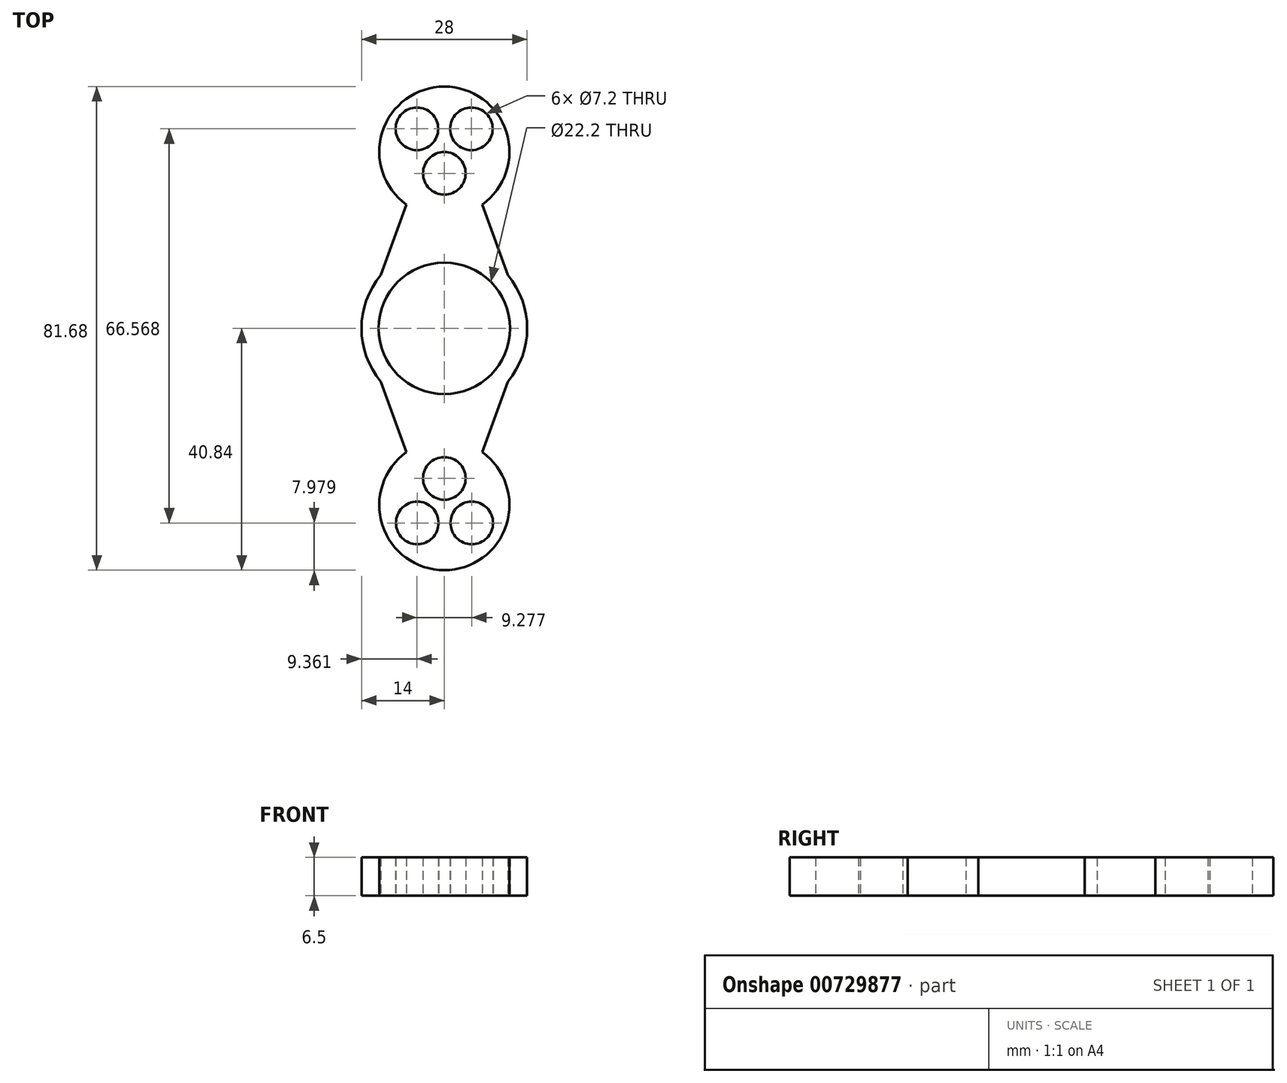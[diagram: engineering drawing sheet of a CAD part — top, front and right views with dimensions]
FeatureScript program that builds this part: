
annotation { "Feature Type Name" : "Feature", "Feature Type Description" : "" }
export const myFeature = defineFeature(function(context is Context, id is Id, definition is map)
    precondition{}
    {
        {
            var Q0;
            Q0=qCreatedBy(makeId("Top.planeOp"),FACE);
            var sketch = newSketch(context, id + "F0", { "sketchPlane" : qUnion([Q0])});
            skCircle(sketch, "E0", {"center": v(0, 0) * mm, "radius": 11.1 * mm});
            skCircle(sketch, "E1", {"center": v(0, 0) * mm, "radius": 14 * mm});
            skLineSegment(sketch, "E2", {"start": v(-14, 0) * mm, "end": v(0, 38.49) * mm});
            skLineSegment(sketch, "E3", {"start": v(0, 38.49) * mm, "end": v(14, 0) * mm});
            skCircle(sketch, "E4", {"center": v(0, 29.84) * mm, "radius": 11 * mm});
            skLineSegment(sketch, "E5", {"start": v(14, 0) * mm, "end": v(0, -38.49) * mm});
            skLineSegment(sketch, "E6", {"start": v(0, -38.49) * mm, "end": v(-14, 0) * mm});
            skCircle(sketch, "E7", {"center": v(0, -29.84) * mm, "radius": 11 * mm});
            skCircle(sketch, "E8", {"center": v(4.58, 33.7) * mm, "radius": 3.6 * mm});
            skCircle(sketch, "E9", {"center": v(-4.64, 33.7) * mm, "radius": 3.6 * mm});
            skCircle(sketch, "E10", {"center": v(0, 26.19) * mm, "radius": 3.6 * mm});
            skCircle(sketch, "E11", {"center": v(-4.58, -32.86) * mm, "radius": 3.6 * mm});
            skCircle(sketch, "E12", {"center": v(4.64, -32.86) * mm, "radius": 3.6 * mm});
            skCircle(sketch, "E13", {"center": v(0, -25.34) * mm, "radius": 3.6 * mm});
            skSolve(sketch);
        }
        {
            var Q0;
            Q0=makeQuery(id+"F0.imprint","IMPRINT",FACE,{"disambiguationData":[TD([[makeQuery(id+"F0.imprint","IMPRINT",EDGE,{"derivedFrom":sQuery(id+"F0.wireOp",EDGE,"E0")}),-1.0]])]});
            var Q1;
            {var subQ0=sQuery(id+"F0.wireOp",EDGE,"E2");var subQ1=sQuery(id+"F0.wireOp",EDGE,"E1");var subQ3=makeQuery(id+"F0.imprint","INTERSECT",VERTEX,{"derivedFrom":[subQ1,subQ0]});Q1=makeQuery(id+"F0.imprint","IMPRINT",FACE,{"disambiguationData":[TD([[makeQuery(id+"F0.imprint","IMPRINT",EDGE,{"disambiguationData":[TD([[subQ3,-1.0]])],"derivedFrom":subQ1}),1.0]])]});}
            var Q2;
            {var subQ0=sQuery(id+"F0.wireOp",EDGE,"E6");var subQ1=sQuery(id+"F0.wireOp",EDGE,"E1");var subQ3=makeQuery(id+"F0.imprint","INTERSECT",VERTEX,{"derivedFrom":[subQ1,subQ0]});Q2=makeQuery(id+"F0.imprint","IMPRINT",FACE,{"disambiguationData":[TD([[makeQuery(id+"F0.imprint","IMPRINT",EDGE,{"disambiguationData":[TD([[subQ3,1.0]])],"derivedFrom":subQ1}),1.0]])]});}
            var Q3;
            {var subQ0=sQuery(id+"F0.wireOp",EDGE,"E5");var subQ1=sQuery(id+"F0.wireOp",EDGE,"E1");var subQ3=makeQuery(id+"F0.imprint","INTERSECT",VERTEX,{"derivedFrom":[subQ1,subQ0]});Q3=makeQuery(id+"F0.imprint","IMPRINT",FACE,{"disambiguationData":[TD([[makeQuery(id+"F0.imprint","IMPRINT",EDGE,{"disambiguationData":[TD([[subQ3,-1.0]])],"derivedFrom":subQ1}),1.0]])]});}
            var Q4;
            {var subQ0=sQuery(id+"F0.wireOp",EDGE,"E3");var subQ1=sQuery(id+"F0.wireOp",EDGE,"E1");var subQ3=makeQuery(id+"F0.imprint","INTERSECT",VERTEX,{"derivedFrom":[subQ1,subQ0]});Q4=makeQuery(id+"F0.imprint","IMPRINT",FACE,{"disambiguationData":[TD([[makeQuery(id+"F0.imprint","IMPRINT",EDGE,{"disambiguationData":[TD([[subQ3,1.0]])],"derivedFrom":subQ1}),1.0]])]});}
            var Q5;
            Q5=makeQuery(id+"F0.imprint","IMPRINT",FACE,{"disambiguationData":[TD([[makeQuery(id+"F0.imprint","IMPRINT",EDGE,{"derivedFrom":sQuery(id+"F0.wireOp",EDGE,"E10")}),-1.0]])]});
            var Q6;
            {var subQ1=sQuery(id+"F0.wireOp",EDGE,"E2");var subQ8=sQuery(id+"F0.wireOp",EDGE,"E4");var subQ11=makeQuery(id+"F0.imprint","INTERSECT",VERTEX,{"derivedFrom":[subQ1,subQ8]});Q6=makeQuery(id+"F0.imprint","IMPRINT",FACE,{"disambiguationData":[TD([[makeQuery(id+"F0.imprint","IMPRINT",EDGE,{"disambiguationData":[TD([[subQ11,-1.0]])],"derivedFrom":subQ1}),1.0]])]});}
            var Q7;
            {var subQ0=sQuery(id+"F0.wireOp",EDGE,"E3");var subQ1=sQuery(id+"F0.wireOp",EDGE,"E1");var subQ2=makeQuery(id+"F0.imprint","INTERSECT",VERTEX,{"derivedFrom":[subQ1,subQ0]});Q7=makeQuery(id+"F0.imprint","IMPRINT",FACE,{"disambiguationData":[TD([[makeQuery(id+"F0.imprint","IMPRINT",EDGE,{"disambiguationData":[TD([[subQ2,-1.0]])],"derivedFrom":subQ1}),-1.0]])]});}
            var Q8;
            Q8=makeQuery(id+"F0.imprint","IMPRINT",FACE,{"disambiguationData":[TD([[makeQuery(id+"F0.imprint","IMPRINT",EDGE,{"derivedFrom":sQuery(id+"F0.wireOp",EDGE,"E13")}),-1.0]])]});
            var Q9;
            {var subQ0=sQuery(id+"F0.wireOp",EDGE,"E6");var subQ1=sQuery(id+"F0.wireOp",EDGE,"E1");var subQ2=makeQuery(id+"F0.imprint","INTERSECT",VERTEX,{"derivedFrom":[subQ1,subQ0]});Q9=makeQuery(id+"F0.imprint","IMPRINT",FACE,{"disambiguationData":[TD([[makeQuery(id+"F0.imprint","IMPRINT",EDGE,{"disambiguationData":[TD([[subQ2,-1.0]])],"derivedFrom":subQ1}),-1.0]])]});}
            var Q10;
            {var subQ1=sQuery(id+"F0.wireOp",EDGE,"E5");var subQ7=sQuery(id+"F0.wireOp",EDGE,"E7");var subQ10=makeQuery(id+"F0.imprint","INTERSECT",VERTEX,{"derivedFrom":[subQ1,subQ7]});Q10=makeQuery(id+"F0.imprint","IMPRINT",FACE,{"disambiguationData":[TD([[makeQuery(id+"F0.imprint","IMPRINT",EDGE,{"disambiguationData":[TD([[subQ10,-1.0]])],"derivedFrom":subQ1}),1.0]])]});}
            extrude(context, id + "F1", {"entities" : qUnion([Q0, Q1, Q2, Q3, Q4, Q5, Q6, Q7, Q8, Q9, Q10]), "depth" : 6.5 * mm, "offsetDistance" : 25 * mm});
        }
    });
